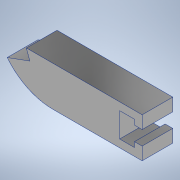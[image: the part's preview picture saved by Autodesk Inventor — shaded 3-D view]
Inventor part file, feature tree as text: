
AUTODESK INVENTOR PART (.ipt)
format: ipt  version: 2022 (Build 260153000, 153)  size: 152,576 bytes
history: native  units: mm
features: extrude x2, fillet x1, sketch x1
ambient origin geometry x8: Origin, YZ Plane, XZ Plane, XY Plane, X Axis, Y Axis, Z Axis, Center Point
bodies: Body1 (feature_tree)
feature tree (4):
  extrude  "Extrusion2"  Depth=23.0mm
  extrude  "Extrusion5"  Depth=3.0mm
  fillet  "Fillet2"  Radius=12.0mm
  sketch  "Sketch8"  dims[d41=5.8mm d48=44.0mm d50=3.0mm d56=12.0mm d57=0.0mm d63=45.0mm d67=15.6mm d71=0.0mm d82=0.0mm d83=0.0mm d87=5.6mm d88=9.6mm d95=4.0mm d97=15.6mm d98=23.0mm d99=35.13673mm d100=19.198622mm]
